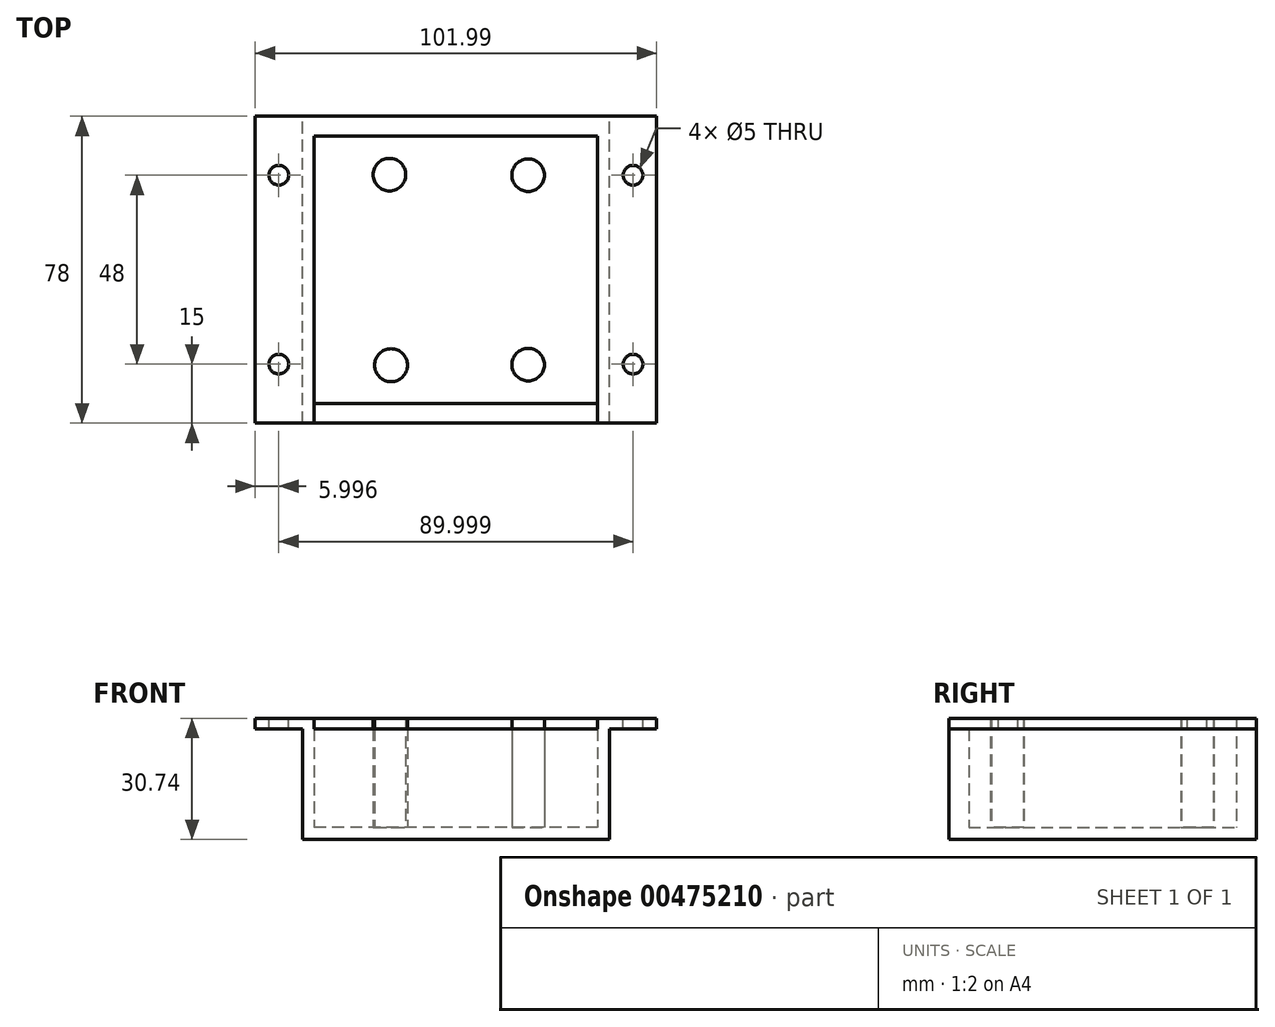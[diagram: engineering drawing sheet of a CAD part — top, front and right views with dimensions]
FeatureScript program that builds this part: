
annotation { "Feature Type Name" : "Feature", "Feature Type Description" : "" }
export const myFeature = defineFeature(function(context is Context, id is Id, definition is map)
    precondition{}
    {
        {
            var Q0;
            Q0=qCreatedBy(makeId("Front.planeOp"),FACE);
            var sketch = newSketch(context, id + "F0", { "sketchPlane" : qUnion([Q0])});
            skLineSegment(sketch, "E0", {"start": v(-2.97, -6.62) * mm, "end": v(-2.97, -9.62) * mm});
            skLineSegment(sketch, "E1", {"start": v(-2.97, -9.62) * mm, "end": v(36.03, -9.62) * mm});
            skLineSegment(sketch, "E2", {"start": v(36.03, -9.62) * mm, "end": v(36.03, 18.38) * mm});
            skLineSegment(sketch, "E3", {"start": v(36.03, 18.38) * mm, "end": v(48.02, 18.38) * mm});
            skLineSegment(sketch, "E4", {"start": v(48.02, 18.38) * mm, "end": v(48.02, 21.12) * mm});
            skLineSegment(sketch, "E5", {"start": v(48.02, 21.12) * mm, "end": v(33.02, 21.12) * mm});
            skLineSegment(sketch, "E6", {"start": v(33.02, 21.12) * mm, "end": v(33.02, -6.62) * mm});
            skLineSegment(sketch, "E7", {"start": v(33.02, -6.62) * mm, "end": v(-2.97, -6.62) * mm});
            skLineSegment(sketch, "E8.MirrorCS", {"start": v(-53.97, 18.38) * mm, "end": v(-53.97, 21.12) * mm});
            skLineSegment(sketch, "E9.MirrorCS", {"start": v(-41.97, -9.62) * mm, "end": v(-41.97, 18.38) * mm});
            skLineSegment(sketch, "E10.MirrorCS", {"start": v(-41.97, 18.38) * mm, "end": v(-53.97, 18.38) * mm});
            skLineSegment(sketch, "E11.MirrorCS", {"start": v(-53.97, 21.12) * mm, "end": v(-38.97, 21.12) * mm});
            skLineSegment(sketch, "E12.MirrorCS", {"start": v(-38.97, 21.12) * mm, "end": v(-38.97, -6.62) * mm});
            skLineSegment(sketch, "E13.MirrorCS", {"start": v(-2.97, -9.62) * mm, "end": v(-41.97, -9.62) * mm});
            skLineSegment(sketch, "E14.MirrorCS", {"start": v(-38.97, -6.62) * mm, "end": v(-2.97, -6.62) * mm});
            skPoint(sketch, "E15.MirrorCS.start.orphan", {"position": v(36.03, 18.38) * mm});
            skSolve(sketch);
        }
        {
            var Q0;
            Q0=qSketchRegion(id+"F0",true);
            extrude(context, id + "F1", {"entities" : qUnion([Q0]), "endBound" : BoundingType.SYMMETRIC, "depth" : 78 * mm});
        }
        {
            var Q0;
            Q0=makeQuery(id+"F1.opExtrude","SWEPT_FACE",FACE,{"disambiguationData":[OSD([sQuery(id+"F0.wireOp",EDGE,"E5")])]});
            var sketch = newSketch(context, id + "F2", { "sketchPlane" : qUnion([Q0])});
            skLineSegment(sketch, "E16", {"start": v(42.02, -39) * mm, "end": v(42.02, 39) * mm, "construction": true});
            skLineSegment(sketch, "E17.0.0", {"start": v(-38.97, 39) * mm, "end": v(-53.97, 39) * mm, "construction": true});
            skLineSegment(sketch, "E17.0.1", {"start": v(-53.97, 39) * mm, "end": v(-53.97, -39) * mm, "construction": true});
            skLineSegment(sketch, "E17.0.2", {"start": v(-53.97, -39) * mm, "end": v(-38.97, -39) * mm, "construction": true});
            skLineSegment(sketch, "E17.0.3", {"start": v(-38.97, -39) * mm, "end": v(-38.97, 39) * mm, "construction": true});
            skLineSegment(sketch, "E18", {"start": v(-47.97, 39) * mm, "end": v(-47.97, -39) * mm, "construction": true});
            skLineSegment(sketch, "E19", {"start": v(-53.97, -24) * mm, "end": v(48.02, -24) * mm, "construction": true});
            skLineSegment(sketch, "E20", {"start": v(48.02, 24) * mm, "end": v(-53.97, 24) * mm, "construction": true});
            skLineSegment(sketch, "E21", {"start": v(48.02, -24) * mm, "end": v(48.02, -39) * mm, "construction": true});
            skLineSegment(sketch, "E22", {"start": v(48.02, 39) * mm, "end": v(48.02, 24) * mm, "construction": true});
            skCircle(sketch, "E23", {"center": v(42.02, -24) * mm, "radius": 2.5 * mm});
            skCircle(sketch, "E24", {"center": v(42.02, 24) * mm, "radius": 2.5 * mm});
            skCircle(sketch, "E25", {"center": v(-47.97, 24) * mm, "radius": 2.5 * mm});
            skCircle(sketch, "E26", {"center": v(-47.97, -24) * mm, "radius": 2.5 * mm});
            skSolve(sketch);
        }
        {
            var Q0;
            Q0=qSketchRegion(id+"F2",true);
            extrude(context, id + "F3", {"entities" : qUnion([Q0]), "operationType" : NewBodyOperationType.REMOVE, "endBound" : BoundingType.UP_TO_NEXT, "oppositeDirection" : true, "depth" : 25 * mm});
        }
        {
            var Q0;
            Q0=makeQuery(id+"F1.opExtrude","SWEPT_FACE",FACE,{"disambiguationData":[OSD([sQuery(id+"F0.wireOp",EDGE,"E7"),sQuery(id+"F0.wireOp",EDGE,"E14.MirrorCS")])]});
            var sketch = newSketch(context, id + "F4", { "sketchPlane" : qUnion([Q0])});
            skCircle(sketch, "E27", {"center": v(15.38, 24) * mm, "radius": 4.14 * mm});
            skCircle(sketch, "E28", {"center": v(15.38, -24.14) * mm, "radius": 4.14 * mm});
            skCircle(sketch, "E29", {"center": v(-19.85, 24.14) * mm, "radius": 4.14 * mm});
            skCircle(sketch, "E30", {"center": v(-19.45, -24.27) * mm, "radius": 4.2 * mm});
            skSolve(sketch);
        }
        {
            var Q0;
            Q0=qSketchRegion(id+"F4",true);
            var Q1;
            Q1=makeQuery(id+"F1.opExtrude","SWEPT_FACE",FACE,{"disambiguationData":[OSD([sQuery(id+"F0.wireOp",EDGE,"E11.MirrorCS")])]});
            extrude(context, id + "F5", {"entities" : qUnion([Q0]), "operationType" : NewBodyOperationType.ADD, "endBound" : BoundingType.UP_TO_SURFACE, "endBoundEntityFace" : qUnion([Q1]), "depth" : 25 * mm});
        }
        {
            var Q0;
            Q0=makeQuery(id+"F1.opExtrude","CAP_FACE",FACE,{"disambiguationData":[OSD([sQuery(id+"F0.wireOp",EDGE,"E1"),sQuery(id+"F0.wireOp",EDGE,"E2"),sQuery(id+"F0.wireOp",EDGE,"E3"),sQuery(id+"F0.wireOp",EDGE,"E4"),sQuery(id+"F0.wireOp",EDGE,"E5"),sQuery(id+"F0.wireOp",EDGE,"E6"),sQuery(id+"F0.wireOp",EDGE,"E7"),sQuery(id+"F0.wireOp",EDGE,"E8.MirrorCS"),sQuery(id+"F0.wireOp",EDGE,"E9.MirrorCS"),sQuery(id+"F0.wireOp",EDGE,"E10.MirrorCS"),sQuery(id+"F0.wireOp",EDGE,"E11.MirrorCS"),sQuery(id+"F0.wireOp",EDGE,"E12.MirrorCS"),sQuery(id+"F0.wireOp",EDGE,"E13.MirrorCS"),sQuery(id+"F0.wireOp",EDGE,"E14.MirrorCS")])],"isStart":false});
            var sketch = newSketch(context, id + "F6", { "sketchPlane" : qUnion([Q0])});
            skLineSegment(sketch, "E31.bottom", {"start": v(36.03, 18.38) * mm, "end": v(-41.97, 18.38) * mm});
            skLineSegment(sketch, "E31.top", {"start": v(36.03, -9.62) * mm, "end": v(-41.97, -9.62) * mm});
            skLineSegment(sketch, "E31.left", {"start": v(36.03, 18.38) * mm, "end": v(36.03, -9.62) * mm});
            skLineSegment(sketch, "E31.right", {"start": v(-41.97, 18.38) * mm, "end": v(-41.97, -9.62) * mm});
            skSolve(sketch);
        }
        {
            var Q0;
            {var subQ5=makeQuery(id+"F1.opExtrude","CAP_EDGE",EDGE,{"disambiguationData":[OSD([sQuery(id+"F0.wireOp",EDGE,"E7"),sQuery(id+"F0.wireOp",EDGE,"E14.MirrorCS")])],"isStart":false});Q0=makeQuery(id+"F6.imprint","IMPRINT",FACE,{"disambiguationData":[TD([[makeQuery(id+"F6.imprint","IMPRINT",EDGE,{"derivedFrom":subQ5}),-1.0]])]});}
            extrude(context, id + "F7", {"entities" : qUnion([Q0]), "operationType" : NewBodyOperationType.ADD, "oppositeDirection" : true, "depth" : 5 * mm});
        }
        {
            var Q0;
            Q0=makeQuery(id+"F1.opExtrude","CAP_FACE",FACE,{"disambiguationData":[OSD([sQuery(id+"F0.wireOp",EDGE,"E1"),sQuery(id+"F0.wireOp",EDGE,"E2"),sQuery(id+"F0.wireOp",EDGE,"E3"),sQuery(id+"F0.wireOp",EDGE,"E4"),sQuery(id+"F0.wireOp",EDGE,"E5"),sQuery(id+"F0.wireOp",EDGE,"E6"),sQuery(id+"F0.wireOp",EDGE,"E7"),sQuery(id+"F0.wireOp",EDGE,"E8.MirrorCS"),sQuery(id+"F0.wireOp",EDGE,"E9.MirrorCS"),sQuery(id+"F0.wireOp",EDGE,"E10.MirrorCS"),sQuery(id+"F0.wireOp",EDGE,"E11.MirrorCS"),sQuery(id+"F0.wireOp",EDGE,"E12.MirrorCS"),sQuery(id+"F0.wireOp",EDGE,"E13.MirrorCS"),sQuery(id+"F0.wireOp",EDGE,"E14.MirrorCS")])],"isStart":true});
            var sketch = newSketch(context, id + "F8", { "sketchPlane" : qUnion([Q0])});
            skLineSegment(sketch, "E32.bottom", {"start": v(-36.03, 21.12) * mm, "end": v(41.97, 21.12) * mm});
            skLineSegment(sketch, "E32.top", {"start": v(-36.03, -9.62) * mm, "end": v(41.97, -9.62) * mm});
            skLineSegment(sketch, "E32.left", {"start": v(-36.03, 21.12) * mm, "end": v(-36.03, -9.62) * mm});
            skLineSegment(sketch, "E32.right", {"start": v(41.97, 21.12) * mm, "end": v(41.97, -9.62) * mm});
            skSolve(sketch);
        }
        {
            var Q0;
            {var subQ1=makeQuery(id+"F1.opExtrude","CAP_EDGE",EDGE,{"disambiguationData":[OSD([sQuery(id+"F0.wireOp",EDGE,"E6")])],"isStart":true});Q0=makeQuery(id+"F8.imprint","IMPRINT",FACE,{"disambiguationData":[TD([[makeQuery(id+"F8.imprint","IMPRINT",EDGE,{"derivedFrom":subQ1}),1.0]])]});}
            extrude(context, id + "F9", {"entities" : qUnion([Q0]), "operationType" : NewBodyOperationType.ADD, "oppositeDirection" : true, "depth" : 5 * mm});
        }
    });
